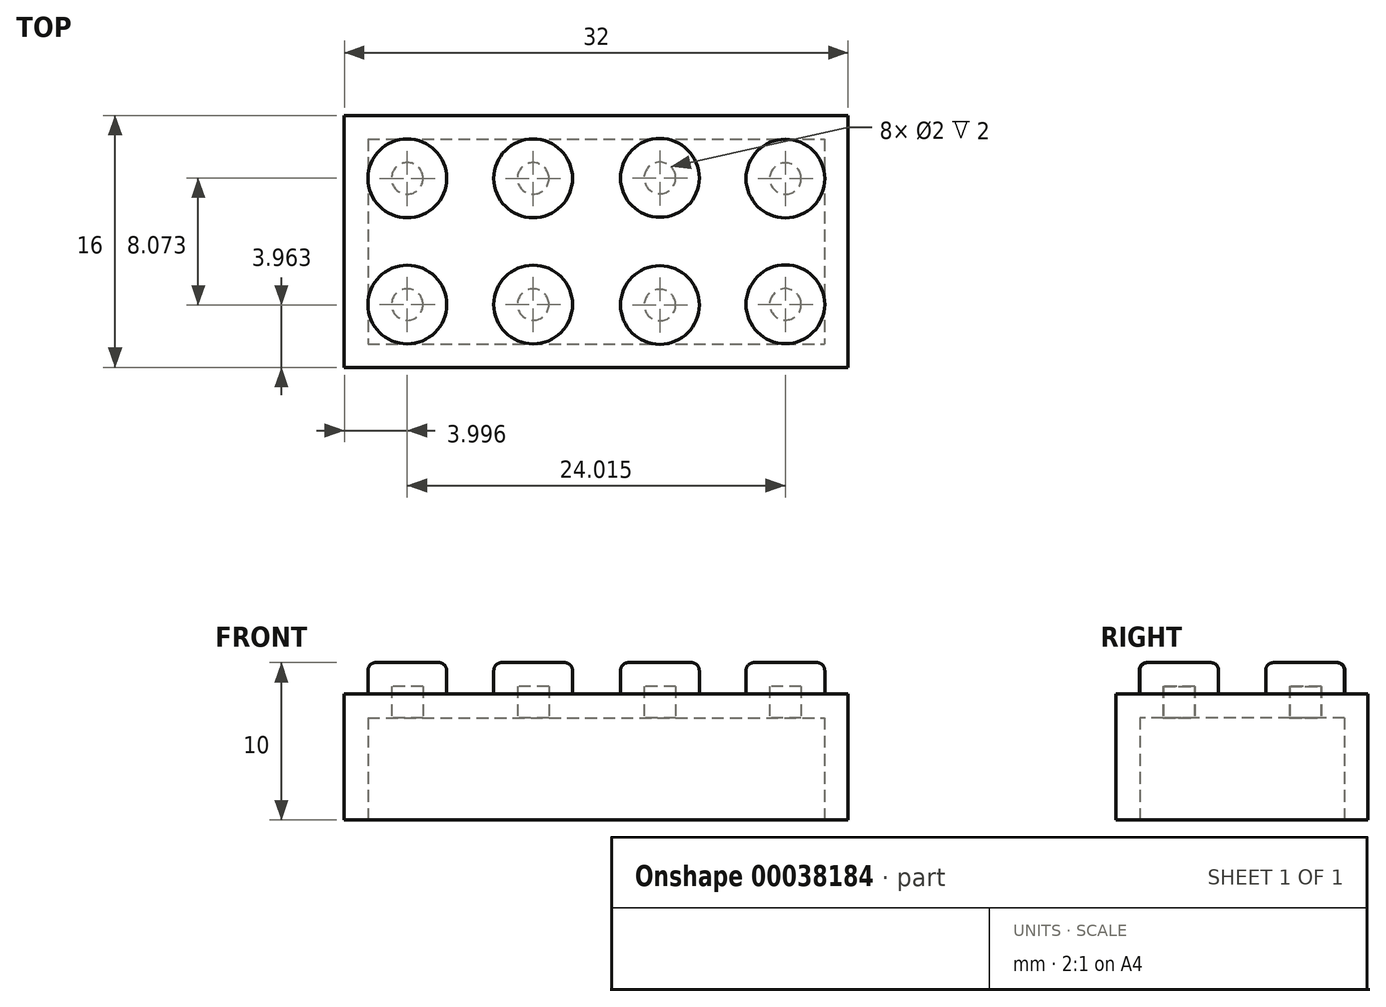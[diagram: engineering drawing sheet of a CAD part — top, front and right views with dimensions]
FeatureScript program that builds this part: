
annotation { "Feature Type Name" : "Feature", "Feature Type Description" : "" }
export const myFeature = defineFeature(function(context is Context, id is Id, definition is map)
    precondition{}
    {
        {
            var Q0;
            Q0=qCreatedBy(makeId("Top.planeOp"),FACE);
            var sketch = newSketch(context, id + "F0", { "sketchPlane" : qUnion([Q0])});
            skLineSegment(sketch, "E0.bottom", {"start": v(-15.83, 9.56) * mm, "end": v(16.17, 9.56) * mm});
            skLineSegment(sketch, "E0.top", {"start": v(-15.83, -6.44) * mm, "end": v(16.17, -6.44) * mm});
            skLineSegment(sketch, "E0.left", {"start": v(-15.83, 9.56) * mm, "end": v(-15.83, -6.44) * mm});
            skLineSegment(sketch, "E0.right", {"start": v(16.17, 9.56) * mm, "end": v(16.17, -6.44) * mm});
            skLineSegment(sketch, "E1", {"start": v(-15.83, 9.56) * mm, "end": v(-15.83, 9.84) * mm, "construction": true});
            skLineSegment(sketch, "E2", {"start": v(-15.83, 9.84) * mm, "end": v(-11.83, 9.84) * mm, "construction": true});
            skLineSegment(sketch, "E3", {"start": v(-11.83, 9.84) * mm, "end": v(-3.83, 9.84) * mm, "construction": true});
            skLineSegment(sketch, "E4", {"start": v(-3.83, 9.84) * mm, "end": v(4.17, 9.84) * mm, "construction": true});
            skLineSegment(sketch, "E5", {"start": v(4.17, 9.84) * mm, "end": v(12.17, 9.84) * mm, "construction": true});
            skLineSegment(sketch, "E6", {"start": v(-15.83, 9.56) * mm, "end": v(-17.16, 9.56) * mm, "construction": true});
            skLineSegment(sketch, "E7", {"start": v(-17.16, 9.56) * mm, "end": v(-17.16, 5.56) * mm, "construction": true});
            skLineSegment(sketch, "E8", {"start": v(-17.16, 5.56) * mm, "end": v(-17.16, 1.56) * mm, "construction": true});
            skLineSegment(sketch, "E9", {"start": v(-17.16, 1.56) * mm, "end": v(-17.16, -6.44) * mm, "construction": true});
            skLineSegment(sketch, "E10", {"start": v(-17.16, 5.56) * mm, "end": v(18.67, 5.56) * mm, "construction": true});
            skLineSegment(sketch, "E11", {"start": v(-11.83, 9.84) * mm, "end": v(-11.83, 3.47) * mm, "construction": true});
            skLineSegment(sketch, "E12", {"start": v(-3.83, 9.84) * mm, "end": v(-3.83, 2.68) * mm, "construction": true});
            skLineSegment(sketch, "E13", {"start": v(4.17, 9.84) * mm, "end": v(4.17, 3.77) * mm, "construction": true});
            skLineSegment(sketch, "E14", {"start": v(12.17, 9.84) * mm, "end": v(12.17, 2.63) * mm, "construction": true});
            skLineSegment(sketch, "E15", {"start": v(-17.16, 1.56) * mm, "end": v(18.42, 1.56) * mm, "construction": true});
            skSolve(sketch);
        }
        {
            var Q0;
            Q0=makeQuery(id+"F0.imprint","IMPRINT",FACE,{"disambiguationData":[TD([[makeQuery(id+"F0.imprint","IMPRINT",EDGE,{"derivedFrom":sQuery(id+"F0.wireOp",EDGE,"E0.bottom")}),-1.0]])]});
            extrude(context, id + "F1", {"entities" : qUnion([Q0]), "depth" : 8 * mm});
        }
        {
            var Q0;
            Q0=qCreatedBy(makeId("Top.planeOp"),FACE);
            cPlane(context, id + "F2", {"entities" : qUnion([Q0]), "cplaneType" : CPlaneType.OFFSET, "offset" : 8 * mm, "width" : 150 * mm, "height" : 150 * mm});
        }
        {
            var Q0;
            Q0=qCreatedBy(id+"F2.planeOp",FACE);
            var sketch = newSketch(context, id + "F3", { "sketchPlane" : qUnion([Q0])});
            skCircle(sketch, "E16", {"center": v(-11.83, 5.57) * mm, "radius": 2.5 * mm});
            skCircle(sketch, "E17", {"center": v(-3.84, 5.57) * mm, "radius": 2.5 * mm});
            skCircle(sketch, "E18", {"center": v(4.2, 5.6) * mm, "radius": 2.5 * mm});
            skCircle(sketch, "E19", {"center": v(12.18, 5.55) * mm, "radius": 2.5 * mm});
            skCircle(sketch, "E20.MirrorC", {"center": v(4.2, -2.48) * mm, "radius": 2.5 * mm});
            skCircle(sketch, "E21.MirrorC", {"center": v(-3.84, -2.45) * mm, "radius": 2.5 * mm});
            skCircle(sketch, "E22.MirrorC", {"center": v(-11.83, -2.45) * mm, "radius": 2.5 * mm});
            skCircle(sketch, "E23.MirrorC", {"center": v(12.18, -2.44) * mm, "radius": 2.5 * mm});
            skSolve(sketch);
        }
        {
            var Q0;
            Q0 = qSketchRegion(id + "F3", true);
            extrude(context, id + "F4", {"entities" : qUnion([Q0]), "operationType" : NewBodyOperationType.ADD, "depth" : 2 * mm});
        }
        {
            var Q0;
            Q0=makeQuery(id+"F4.opExtrude","CAP_EDGE",EDGE,{"disambiguationData":[OSD([sQuery(id+"F3.wireOp",EDGE,"E19")])],"isStart":false});
            var Q1;
            Q1=makeQuery(id+"F4.opExtrude","CAP_FACE",FACE,{"disambiguationData":[OSD([sQuery(id+"F3.wireOp",EDGE,"E18")])],"isStart":false});
            var Q2;
            Q2=makeQuery(id+"F4.opExtrude","CAP_EDGE",EDGE,{"disambiguationData":[OSD([sQuery(id+"F3.wireOp",EDGE,"E17")])],"isStart":false});
            var Q3;
            Q3=makeQuery(id+"F4.opExtrude","CAP_EDGE",EDGE,{"disambiguationData":[OSD([sQuery(id+"F3.wireOp",EDGE,"E16")])],"isStart":false});
            var Q4;
            Q4=makeQuery(id+"F4.opExtrude","CAP_EDGE",EDGE,{"disambiguationData":[OSD([sQuery(id+"F3.wireOp",EDGE,"E22.MirrorC")])],"isStart":false});
            var Q5;
            Q5=makeQuery(id+"F4.opExtrude","CAP_EDGE",EDGE,{"disambiguationData":[OSD([sQuery(id+"F3.wireOp",EDGE,"E21.MirrorC")])],"isStart":false});
            var Q6;
            Q6=makeQuery(id+"F4.opExtrude","CAP_FACE",FACE,{"disambiguationData":[OSD([sQuery(id+"F3.wireOp",EDGE,"E20.MirrorC")])],"isStart":false});
            var Q7;
            Q7=makeQuery(id+"F4.opExtrude","CAP_FACE",FACE,{"disambiguationData":[OSD([sQuery(id+"F3.wireOp",EDGE,"E23.MirrorC")])],"isStart":false});
            fillet(context, id + "F5", {"entities" : qUnion([Q0, Q1, Q2, Q3, Q4, Q5, Q6, Q7]), "radius" : 0.5 * mm, "tangentPropagation" : true, "allowEdgeOverflow" : false});
        }
        {
            var Q0;
            Q0=makeQuery(id+"F1.opExtrude","CAP_FACE",FACE,{"disambiguationData":[OSD([sQuery(id+"F0.wireOp",EDGE,"E0.bottom"),sQuery(id+"F0.wireOp",EDGE,"E0.top"),sQuery(id+"F0.wireOp",EDGE,"E0.left"),sQuery(id+"F0.wireOp",EDGE,"E0.right")])],"isStart":true});
            shell(context, id + "F6", {"entities" : qUnion([Q0]), "thickness" : 1.5 * mm});
        }
    });
